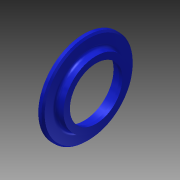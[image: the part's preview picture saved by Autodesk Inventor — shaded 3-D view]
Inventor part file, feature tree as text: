
AUTODESK INVENTOR PART (.ipt)
format: ipt  version: 2014 (Build 180170000, 170)  size: 145,408 bytes
history: native  units: in
note: dims shown in document units (in); Inventor stores cm internally (conversion verified against a paired STEP export)
features: reference x8, chamfer x2, sketch x2, revolve x1, plane x1, extrude x1
ambient origin geometry x8: Origin, YZ Plane, XZ Plane, XY Plane, X Axis, Y Axis, Z Axis, Center Point
bodies: Solid1 (feature_tree)
feature tree (15):
  revolve  "Revolution1"  [1 undecoded]
  chamfer  "Chamfer1"  Distance=0.01in
  plane  "Work Plane1"
  extrude  "Extrusion1"  Depth=0.1in
  chamfer  "Chamfer2"  Distance=0.1in
  sketch  "Sketch1"  dims[d0=0.025in d1=0.025in]
  reference  "Reference1"
  reference  "Reference2"
  reference  "Reference3"
  reference  "Reference4"
  reference  "Reference5"
  reference  "Reference6"
  reference  "Reference7"
  reference  "Reference8"
  sketch  "Sketch2"  dims[d2=0.3in d3=0.01in d4=0.01in d5=0.1in d6=0.1in d7=0.05in d9=0.5in d10=0.1001in d11=90.0deg d12=0.05in d13=0.125in d14=45.0deg d15=0.0in d16=0.0in d17=0.05in d18=0.125in d19=45.0deg]
note: 1 required parameter value undecoded (feature->parameter linkage not recoverable at this tier; creation-order binding heuristic only, values carry confidence <= 0.55)
